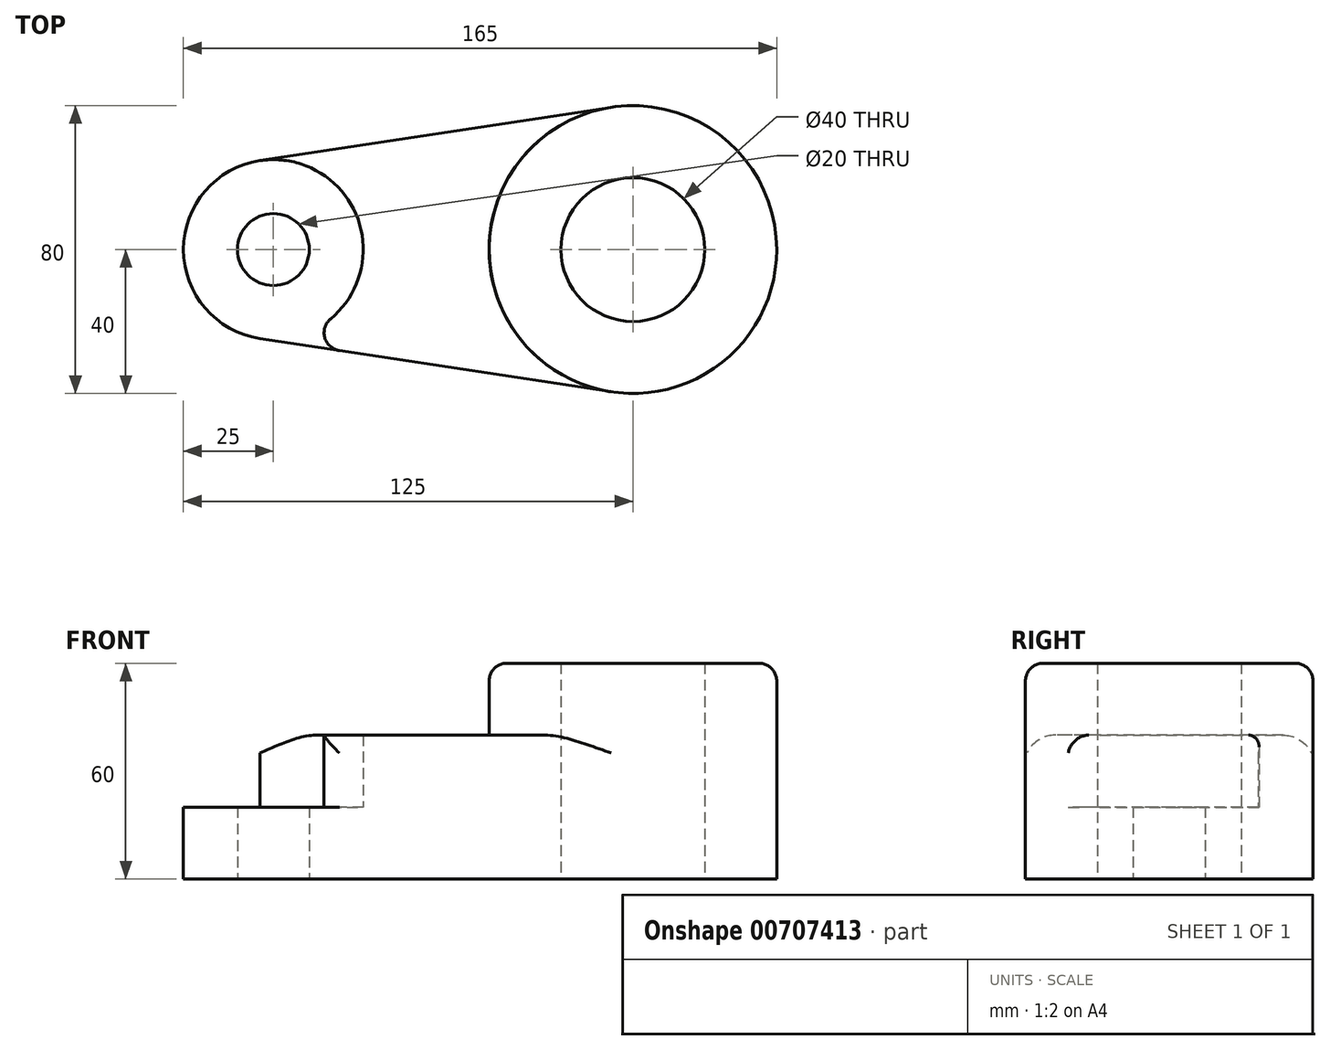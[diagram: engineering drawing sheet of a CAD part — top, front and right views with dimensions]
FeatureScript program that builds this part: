
annotation { "Feature Type Name" : "Feature", "Feature Type Description" : "" }
export const myFeature = defineFeature(function(context is Context, id is Id, definition is map)
    precondition{}
    {
        {
            var Q0;
            Q0=qCreatedBy(makeId("Top.planeOp"),FACE);
            var sketch = newSketch(context, id + "F0", { "sketchPlane" : qUnion([Q0])});
            skCircle(sketch, "E0", {"center": v(-50, 0) * mm, "radius": 25 * mm});
            skCircle(sketch, "E1", {"center": v(-50, 0) * mm, "radius": 10 * mm});
            skCircle(sketch, "E2", {"center": v(50, 0) * mm, "radius": 40 * mm});
            skCircle(sketch, "E3", {"center": v(50, 0) * mm, "radius": 20 * mm});
            skPoint(sketch, "E4.start.orphan", {"position": v(-53.75, 24.72) * mm});
            skLineSegment(sketch, "E5", {"start": v(-53.75, -24.72) * mm, "end": v(44, -39.55) * mm});
            skLineSegment(sketch, "E6", {"start": v(-53.75, 24.72) * mm, "end": v(44, 39.55) * mm});
            skSolve(sketch);
        }
        {
            var Q0;
            Q0=makeQuery(id+"F0.imprint","IMPRINT",FACE,{"disambiguationData":[TD([[makeQuery(id+"F0.imprint","IMPRINT",EDGE,{"derivedFrom":sQuery(id+"F0.wireOp",EDGE,"E2")}),1.0]])]});
            extrude(context, id + "F1", {"entities" : qUnion([Q0]), "depth" : 60 * mm, "offsetDistance" : 25 * mm});
        }
        {
            var Q0;
            Q0=makeQuery(id+"F1.opExtrude","CAP_EDGE",EDGE,{"disambiguationData":[OSD([sQuery(id+"F0.wireOp",EDGE,"E2")])],"isStart":false});
            fillet(context, id + "F2", {"entities" : qUnion([Q0]), "radius" : 5 * mm, "tangentPropagation" : true, "allowEdgeOverflow" : false});
        }
        {
            var Q0;
            Q0=makeQuery(id+"F0.imprint","IMPRINT",FACE,{"disambiguationData":[TD([[makeQuery(id+"F0.imprint","IMPRINT",EDGE,{"derivedFrom":sQuery(id+"F0.wireOp",EDGE,"E1")}),-1.0]])]});
            extrude(context, id + "F3", {"entities" : qUnion([Q0]), "depth" : 20 * mm, "offsetDistance" : 25 * mm});
        }
        {
            var Q0;
            {var subQ0=sQuery(id+"F0.wireOp",EDGE,"E5");Q0=makeQuery(id+"F0.imprint","IMPRINT",FACE,{"disambiguationData":[TD([[makeQuery(id+"F0.imprint","IMPRINT",EDGE,{"derivedFrom":subQ0}),1.0]])]});}
            extrude(context, id + "F4", {"entities" : qUnion([Q0]), "depth" : 40 * mm, "offsetDistance" : 25 * mm});
        }
        {
            var Q0;
            Q0=makeQuery(id+"F4.opExtrude","CAP_EDGE",EDGE,{"disambiguationData":[OSD([sQuery(id+"F0.wireOp",EDGE,"E6")])],"isStart":false});
            fillet(context, id + "F5", {"entities" : qUnion([Q0]), "radius" : 5 * mm, "tangentPropagation" : true, "allowEdgeOverflow" : false});
        }
        {
            var Q0;
            Q0=makeQuery(id+"F4.opExtrude","CAP_EDGE",EDGE,{"disambiguationData":[OSD([sQuery(id+"F0.wireOp",EDGE,"E5")])],"isStart":false});
            fillet(context, id + "F6", {"entities" : qUnion([Q0]), "radius" : 5 * mm, "tangentPropagation" : true, "allowEdgeOverflow" : false});
        }
        {
            var Q0;
            Q0=makeQuery(id+"F1.opExtrude","SWEPT_BODY",BODY,{"disambiguationData":[OSD([sQuery(id+"F0.wireOp",EDGE,"E2"),sQuery(id+"F0.wireOp",EDGE,"E3")])]});
            var Q1;
            Q1=makeQuery(id+"F3.opExtrude","SWEPT_BODY",BODY,{"disambiguationData":[OSD([sQuery(id+"F0.wireOp",EDGE,"E0"),sQuery(id+"F0.wireOp",EDGE,"E1")])]});
            var Q2;
            Q2=makeQuery(id+"F4.opExtrude","SWEPT_BODY",BODY,{"disambiguationData":[OSD([sQuery(id+"F0.wireOp",EDGE,"E0"),sQuery(id+"F0.wireOp",EDGE,"E2"),sQuery(id+"F0.wireOp",EDGE,"E5"),sQuery(id+"F0.wireOp",EDGE,"E6")])]});
            booleanBodies(context, id + "F7", {"operationType" : BooleanOperationType.UNION, "tools" : qUnion([Q0, Q1, Q2])});
        }
        {
            var Q0;
            {var subQ0=sQuery(id+"F0.wireOp",EDGE,"E0");var subQ1=sQuery(id+"F0.wireOp",EDGE,"E5");Q0=makeQuery(id+"F7.opBoolean","SPLIT",EDGE,{"disambiguationData":[topologyDisambiguationEdgeConnected([makeQuery(id+"F4.opExtrude","SWEPT_FACE",FACE,{"disambiguationData":[OSD([subQ0])]})])],"derivedFrom":makeQuery(id+"F4.opExtrude","SWEPT_EDGE",EDGE,{"disambiguationData":[OSD([subQ0,subQ1])]})});}
            var Q1;
            Q1=makeQuery(id+"F4.opExtrude","CAP_EDGE",EDGE,{"disambiguationData":[OSD([sQuery(id+"F0.wireOp",EDGE,"E2")])],"isStart":false});
            fillet(context, id + "F8", {"entities" : qUnion([Q0, Q1]), "radius" : 5 * mm, "tangentPropagation" : true, "allowEdgeOverflow" : false});
        }
    });
